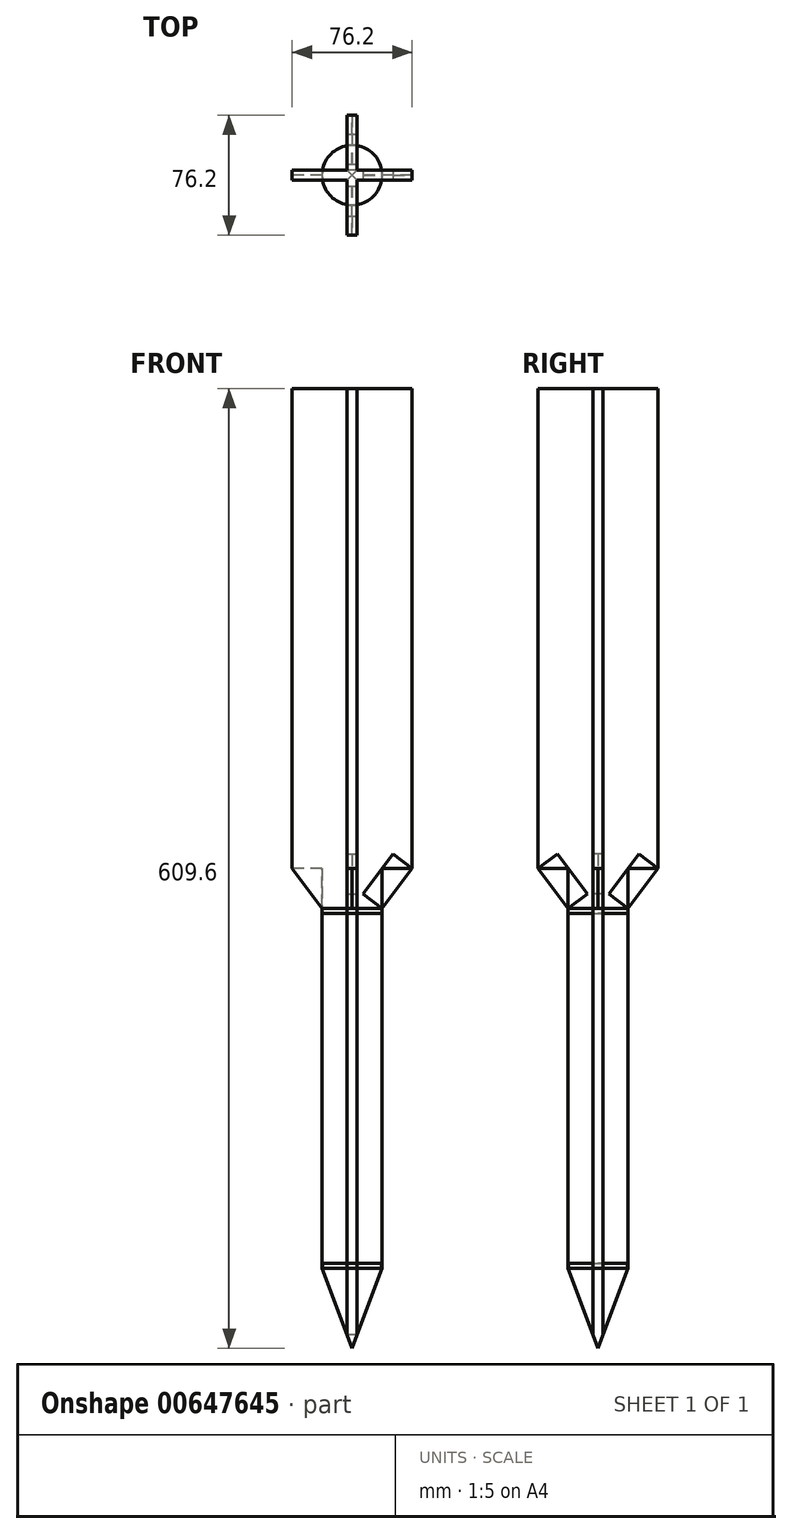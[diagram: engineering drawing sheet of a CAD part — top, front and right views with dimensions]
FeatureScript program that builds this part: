
annotation { "Feature Type Name" : "Feature", "Feature Type Description" : "" }
export const myFeature = defineFeature(function(context is Context, id is Id, definition is map)
    precondition{}
    {
        {
            var Q0;
            Q0=qCreatedBy(makeId("Top.planeOp"),FACE);
            var sketch = newSketch(context, id + "F0", { "sketchPlane" : qUnion([Q0])});
            skLineSegment(sketch, "E0.bottom", {"start": v(3.18, 38.1) * mm, "end": v(-3.17, 38.1) * mm});
            skLineSegment(sketch, "E0.top", {"start": v(3.18, -38.1) * mm, "end": v(-3.18, -38.1) * mm});
            skLineSegment(sketch, "E0.left", {"start": v(3.18, 38.1) * mm, "end": v(3.18, -38.1) * mm});
            skLineSegment(sketch, "E0.right", {"start": v(-3.17, 38.1) * mm, "end": v(-3.18, -38.1) * mm});
            skPoint(sketch, "E0.middle", {"position": v(0, 0) * mm});
            skLineSegment(sketch, "E1.bottom", {"start": v(38.1, -3.17) * mm, "end": v(-38.1, -3.18) * mm});
            skLineSegment(sketch, "E1.top", {"start": v(38.1, 3.18) * mm, "end": v(-38.1, 3.18) * mm});
            skLineSegment(sketch, "E1.left", {"start": v(38.1, -3.17) * mm, "end": v(38.1, 3.18) * mm});
            skLineSegment(sketch, "E1.right", {"start": v(-38.1, -3.18) * mm, "end": v(-38.1, 3.18) * mm});
            skSolve(sketch);
        }
        {
            var Q0;
            {var subQ0=sQuery(id+"F0.wireOp",EDGE,"E0.bottom");Q0=makeQuery(id+"F0.imprint","IMPRINT",FACE,{"disambiguationData":[TD([[makeQuery(id+"F0.imprint","IMPRINT",EDGE,{"derivedFrom":subQ0}),1.0]])]});}
            var Q1;
            {var subQ5=sQuery(id+"F0.wireOp",EDGE,"E1.right");Q1=makeQuery(id+"F0.imprint","IMPRINT",FACE,{"disambiguationData":[TD([[makeQuery(id+"F0.imprint","IMPRINT",EDGE,{"derivedFrom":subQ5}),-1.0]])]});}
            var Q2;
            {var subQ0=sQuery(id+"F0.wireOp",EDGE,"E0.top");Q2=makeQuery(id+"F0.imprint","IMPRINT",FACE,{"disambiguationData":[TD([[makeQuery(id+"F0.imprint","IMPRINT",EDGE,{"derivedFrom":subQ0}),-1.0]])]});}
            var Q3;
            {var subQ0=sQuery(id+"F0.wireOp",EDGE,"E1.top");var subQ1=sQuery(id+"F0.wireOp",EDGE,"E0.left");var subQ2=makeQuery(id+"F0.imprint","INTERSECT",VERTEX,{"derivedFrom":[subQ1,subQ0]});Q3=makeQuery(id+"F0.imprint","IMPRINT",FACE,{"disambiguationData":[TD([[makeQuery(id+"F0.imprint","IMPRINT",EDGE,{"disambiguationData":[TD([[subQ2,-1.0]])],"derivedFrom":subQ1}),-1.0]])]});}
            var Q4;
            {var subQ5=sQuery(id+"F0.wireOp",EDGE,"E1.left");Q4=makeQuery(id+"F0.imprint","IMPRINT",FACE,{"disambiguationData":[TD([[makeQuery(id+"F0.imprint","IMPRINT",EDGE,{"derivedFrom":subQ5}),1.0]])]});}
            extrude(context, id + "F1", {"entities" : qUnion([Q0, Q1, Q2, Q3, Q4]), "depth" : 304.8 * mm, "offsetDistance" : 25.4 * mm});
        }
        {
            var Q0;
            Q0=qCreatedBy(makeId("Top.planeOp"),FACE);
            var sketch = newSketch(context, id + "F2", { "sketchPlane" : qUnion([Q0])});
            skLineSegment(sketch, "E2.bottom", {"start": v(19.05, 3.18) * mm, "end": v(-19.05, 3.17) * mm});
            skLineSegment(sketch, "E2.top", {"start": v(19.05, -3.17) * mm, "end": v(-19.05, -3.18) * mm});
            skLineSegment(sketch, "E2.left", {"start": v(19.05, 3.18) * mm, "end": v(19.05, -3.17) * mm});
            skLineSegment(sketch, "E2.right", {"start": v(-19.05, 3.17) * mm, "end": v(-19.05, -3.18) * mm});
            skPoint(sketch, "E2.middle", {"position": v(0, 0) * mm});
            skLineSegment(sketch, "E3.bottom", {"start": v(3.18, -19.05) * mm, "end": v(-3.18, -19.05) * mm});
            skLineSegment(sketch, "E3.top", {"start": v(3.18, 19.05) * mm, "end": v(-3.17, 19.05) * mm});
            skLineSegment(sketch, "E3.left", {"start": v(3.18, -19.05) * mm, "end": v(3.18, 19.05) * mm});
            skLineSegment(sketch, "E3.right", {"start": v(-3.18, -19.05) * mm, "end": v(-3.17, 19.05) * mm});
            skSolve(sketch);
        }
        {
            var Q0;
            {var subQ0=sQuery(id+"F2.wireOp",EDGE,"E2.left");Q0=makeQuery(id+"F2.imprint","IMPRINT",FACE,{"disambiguationData":[TD([[makeQuery(id+"F2.imprint","IMPRINT",EDGE,{"derivedFrom":subQ0}),-1.0]])]});}
            var Q1;
            {var subQ0=sQuery(id+"F2.wireOp",EDGE,"E2.right");Q1=makeQuery(id+"F2.imprint","IMPRINT",FACE,{"disambiguationData":[TD([[makeQuery(id+"F2.imprint","IMPRINT",EDGE,{"derivedFrom":subQ0}),1.0]])]});}
            var Q2;
            {var subQ5=sQuery(id+"F2.wireOp",EDGE,"E3.top");Q2=makeQuery(id+"F2.imprint","IMPRINT",FACE,{"disambiguationData":[TD([[makeQuery(id+"F2.imprint","IMPRINT",EDGE,{"derivedFrom":subQ5}),1.0]])]});}
            var Q3;
            {var subQ5=sQuery(id+"F2.wireOp",EDGE,"E3.bottom");Q3=makeQuery(id+"F2.imprint","IMPRINT",FACE,{"disambiguationData":[TD([[makeQuery(id+"F2.imprint","IMPRINT",EDGE,{"derivedFrom":subQ5}),-1.0]])]});}
            var Q4;
            {var subQ0=sQuery(id+"F2.wireOp",EDGE,"E3.left");var subQ1=sQuery(id+"F2.wireOp",EDGE,"E2.bottom");var subQ2=makeQuery(id+"F2.imprint","INTERSECT",VERTEX,{"derivedFrom":[subQ1,subQ0]});Q4=makeQuery(id+"F2.imprint","IMPRINT",FACE,{"disambiguationData":[TD([[makeQuery(id+"F2.imprint","IMPRINT",EDGE,{"disambiguationData":[TD([[subQ2,-1.0]])],"derivedFrom":subQ1}),1.0]])]});}
            extrude(context, id + "F3", {"entities" : qUnion([Q0, Q1, Q2, Q3, Q4]), "oppositeDirection" : true, "depth" : 254 * mm, "offsetDistance" : 25.4 * mm});
        }
        {
            var Q0;
            Q0=qCreatedBy(makeId("Front.planeOp"),FACE);
            var sketch = newSketch(context, id + "F4", { "sketchPlane" : qUnion([Q0])});
            skLineSegment(sketch, "E4", {"start": v(38.1, 0) * mm, "end": v(19.07, -25.4) * mm});
            skSolve(sketch);
        }
        {
            var Q0;
            Q0=sQuery(id+"F4.wireOp",EDGE,"E4");
            extrude(context, id + "F5", {"bodyType" : ToolBodyType.SURFACE, "surfaceEntities" : qUnion([Q0]), "depth" : 3.17 * mm, "offsetDistance" : 25.4 * mm});
        }
        {
            var Q0;
            Q0=makeQuery(id+"F5.opExtrude","SWEPT_FACE",FACE,{"disambiguationData":[OSD([sQuery(id+"F4.wireOp",EDGE,"E4")])]});
            extrude(context, id + "F6", {"entities" : qUnion([Q0]), "depth" : 15.24 * mm, "offsetDistance" : 25.4 * mm});
        }
        {
            var Q0;
            {var subQ0=sQuery(id+"F4.wireOp",EDGE,"E4");Q0=makeQuery(id+"F6.opExtrude","SWEPT_FACE",FACE,{"disambiguationData":[OSD([subQ0]),TDD([makeQuery(id+"F5.opExtrude","CAP_EDGE",EDGE,{"disambiguationData":[OSD([subQ0])],"isStart":true})])]});}
            extrude(context, id + "F7", {"entities" : qUnion([Q0]), "depth" : 3.17 * mm, "offsetDistance" : 25.4 * mm});
        }
        {
            var Q0;
            Q0=qCreatedBy(makeId("Front.planeOp"),FACE);
            var sketch = newSketch(context, id + "F8", { "sketchPlane" : qUnion([Q0])});
            skLineSegment(sketch, "E5", {"start": v(-38.1, 0) * mm, "end": v(-18.93, -25.4) * mm});
            skSolve(sketch);
        }
        {
            var Q0;
            Q0 = qSketchRegion(id + "F8", true);
            var Q1;
            Q1=sQuery(id+"F8.wireOp",EDGE,"E5");
            extrude(context, id + "F9", {"entities" : qUnion([Q0]), "bodyType" : ToolBodyType.SURFACE, "surfaceEntities" : qUnion([Q1]), "depth" : 3.17 * mm, "offsetDistance" : 25.4 * mm});
        }
        {
            var Q0;
            Q0=makeQuery(id+"F9.opExtrude","SWEPT_FACE",FACE,{"disambiguationData":[OSD([sQuery(id+"F8.wireOp",EDGE,"E5")])]});
            extrude(context, id + "F10", {"entities" : qUnion([Q0]), "operationType" : NewBodyOperationType.ADD, "oppositeDirection" : true, "depth" : 15.24 * mm, "offsetDistance" : 25.4 * mm});
        }
        {
            var Q0;
            {var subQ0=sQuery(id+"F8.wireOp",EDGE,"E5");Q0=makeQuery(id+"F10.opExtrude","SWEPT_FACE",FACE,{"disambiguationData":[OSD([subQ0]),TDD([makeQuery(id+"F9.opExtrude","CAP_EDGE",EDGE,{"disambiguationData":[OSD([subQ0])],"isStart":true})])]});}
            extrude(context, id + "F11", {"entities" : qUnion([Q0]), "depth" : 3.17 * mm, "offsetDistance" : 25.4 * mm});
        }
        {
            var Q0;
            Q0=qCreatedBy(makeId("Right.planeOp"),FACE);
            var sketch = newSketch(context, id + "F12", { "sketchPlane" : qUnion([Q0])});
            skLineSegment(sketch, "E6", {"start": v(38.1, 0) * mm, "end": v(19.05, -25.4) * mm});
            skLineSegment(sketch, "E7", {"start": v(-38.1, 0) * mm, "end": v(-19.05, -25.4) * mm});
            skSolve(sketch);
        }
        {
            var Q0;
            Q0 = qSketchRegion(id + "F12", true);
            var Q1;
            Q1=sQuery(id+"F12.wireOp",EDGE,"E6");
            extrude(context, id + "F13", {"entities" : qUnion([Q0]), "bodyType" : ToolBodyType.SURFACE, "surfaceEntities" : qUnion([Q1]), "depth" : 3.17 * mm, "offsetDistance" : 25.4 * mm});
        }
        {
            var Q0;
            Q0=makeQuery(id+"F13.opExtrude","SWEPT_FACE",FACE,{"disambiguationData":[OSD([sQuery(id+"F12.wireOp",EDGE,"E6")])]});
            extrude(context, id + "F14", {"entities" : qUnion([Q0]), "depth" : 15.24 * mm, "offsetDistance" : 25.4 * mm});
        }
        {
            var Q0;
            {var subQ0=sQuery(id+"F12.wireOp",EDGE,"E6");Q0=makeQuery(id+"F14.opExtrude","SWEPT_FACE",FACE,{"disambiguationData":[OSD([subQ0]),TDD([makeQuery(id+"F13.opExtrude","CAP_EDGE",EDGE,{"disambiguationData":[OSD([subQ0])],"isStart":true})])]});}
            extrude(context, id + "F15", {"entities" : qUnion([Q0]), "depth" : 3.17 * mm, "offsetDistance" : 25.4 * mm});
        }
        {
            var Q0;
            Q0=sQuery(id+"F12.wireOp",EDGE,"E7");
            extrude(context, id + "F16", {"bodyType" : ToolBodyType.SURFACE, "surfaceEntities" : qUnion([Q0]), "depth" : 3.17 * mm, "offsetDistance" : 25.4 * mm});
        }
        {
            var Q0;
            Q0=makeQuery(id+"F16.opExtrude","SWEPT_FACE",FACE,{"disambiguationData":[OSD([sQuery(id+"F12.wireOp",EDGE,"E7")])]});
            extrude(context, id + "F17", {"entities" : qUnion([Q0]), "oppositeDirection" : true, "depth" : 15.24 * mm, "offsetDistance" : 25.4 * mm});
        }
        {
            var Q0;
            {var subQ0=sQuery(id+"F12.wireOp",EDGE,"E7");Q0=makeQuery(id+"F17.opExtrude","SWEPT_FACE",FACE,{"disambiguationData":[OSD([subQ0]),TDD([makeQuery(id+"F16.opExtrude","CAP_EDGE",EDGE,{"disambiguationData":[OSD([subQ0])],"isStart":true})])]});}
            extrude(context, id + "F18", {"entities" : qUnion([Q0]), "depth" : 3.17 * mm, "offsetDistance" : 25.4 * mm});
        }
        {
            var Q0;
            Q0=qCreatedBy(makeId("Top.planeOp"),FACE);
            var sketch = newSketch(context, id + "F19", { "sketchPlane" : qUnion([Q0])});
            skCircle(sketch, "E8", {"center": v(0, 0) * mm, "radius": 19.05 * mm});
            skSolve(sketch);
        }
        {
            var Q0;
            Q0=makeQuery(id+"F19.imprint","IMPRINT",FACE,{"disambiguationData":[TD([[makeQuery(id+"F19.imprint","IMPRINT",EDGE,{"derivedFrom":sQuery(id+"F19.wireOp",EDGE,"E8")}),1.0]])]});
            extrude(context, id + "F20", {"entities" : qUnion([Q0]), "oppositeDirection" : true, "depth" : 250.82 * mm, "offsetDistance" : 25.4 * mm, "hasSecondDirection" : true, "secondDirectionOppositeDirection" : true, "secondDirectionDepth" : 28.57 * mm});
        }
        {
            var Q0;
            Q0=qCreatedBy(makeId("Top.planeOp"),FACE);
            var sketch = newSketch(context, id + "F21", { "sketchPlane" : qUnion([Q0])});
            skCircle(sketch, "E9", {"center": v(0, 0) * mm, "radius": 19.05 * mm});
            skSolve(sketch);
        }
        {
            var Q0;
            Q0=makeQuery(id+"F21.imprint","IMPRINT",FACE,{"disambiguationData":[TD([[makeQuery(id+"F21.imprint","IMPRINT",EDGE,{"derivedFrom":sQuery(id+"F21.wireOp",EDGE,"E9")}),1.0]])]});
            extrude(context, id + "F22", {"entities" : qUnion([Q0]), "oppositeDirection" : true, "depth" : 28.57 * mm, "offsetDistance" : 25.4 * mm, "hasSecondDirection" : true, "secondDirectionOppositeDirection" : true, "secondDirectionDepth" : 25.4 * mm});
        }
        {
            var Q0;
            Q0=qCreatedBy(makeId("Top.planeOp"),FACE);
            var sketch = newSketch(context, id + "F23", { "sketchPlane" : qUnion([Q0])});
            skCircle(sketch, "E10", {"center": v(0, 0) * mm, "radius": 19.05 * mm});
            skSolve(sketch);
        }
        {
            var Q0;
            Q0=makeQuery(id+"F23.imprint","IMPRINT",FACE,{"disambiguationData":[TD([[makeQuery(id+"F23.imprint","IMPRINT",EDGE,{"derivedFrom":sQuery(id+"F23.wireOp",EDGE,"E10")}),1.0]])]});
            extrude(context, id + "F24", {"entities" : qUnion([Q0]), "oppositeDirection" : true, "depth" : 254 * mm, "offsetDistance" : 25.4 * mm, "hasSecondDirection" : true, "secondDirectionOppositeDirection" : true, "secondDirectionDepth" : 250.82 * mm});
        }
        {
            var Q0;
            Q0=qCreatedBy(makeId("Front.planeOp"),FACE);
            var sketch = newSketch(context, id + "F25", { "sketchPlane" : qUnion([Q0])});
            skLineSegment(sketch, "E11", {"start": v(19.05, -254) * mm, "end": v(0, -304.8) * mm});
            skLineSegment(sketch, "E12", {"start": v(0, -304.8) * mm, "end": v(-19.05, -254) * mm});
            skLineSegment(sketch, "E13", {"start": v(19.05, -254) * mm, "end": v(-19.05, -254) * mm});
            skSolve(sketch);
        }
        {
            var Q0;
            Q0 = qSketchRegion(id + "F25", true);
            extrude(context, id + "F26", {"entities" : qUnion([Q0]), "operationType" : NewBodyOperationType.ADD, "depth" : 3.17 * mm, "offsetDistance" : 25.4 * mm, "hasSecondDirection" : true, "secondDirectionOppositeDirection" : true, "secondDirectionDepth" : 3.17 * mm});
        }
        {
            var Q0;
            Q0=qCreatedBy(makeId("Right.planeOp"),FACE);
            var sketch = newSketch(context, id + "F27", { "sketchPlane" : qUnion([Q0])});
            skLineSegment(sketch, "E14", {"start": v(-19.05, -254) * mm, "end": v(0, -304.8) * mm});
            skLineSegment(sketch, "E15", {"start": v(0, -304.8) * mm, "end": v(19.05, -253.96) * mm});
            skLineSegment(sketch, "E16", {"start": v(19.05, -253.96) * mm, "end": v(-19.05, -254) * mm});
            skSolve(sketch);
        }
        {
            var Q0;
            Q0 = qSketchRegion(id + "F27", true);
            extrude(context, id + "F28", {"entities" : qUnion([Q0]), "operationType" : NewBodyOperationType.ADD, "depth" : 3.17 * mm, "offsetDistance" : 25.4 * mm, "hasSecondDirection" : true, "secondDirectionOppositeDirection" : true, "secondDirectionDepth" : 3.17 * mm});
        }
        {
            var Q0;
            Q0=qCreatedBy(makeId("Front.planeOp"),FACE);
            var sketch = newSketch(context, id + "F29", { "sketchPlane" : qUnion([Q0])});
            skLineSegment(sketch, "E17", {"start": v(19.05, -254) * mm, "end": v(0, -304.8) * mm});
            skLineSegment(sketch, "E18", {"start": v(0, -304.8) * mm, "end": v(14.5, -306.95) * mm});
            skLineSegment(sketch, "E19", {"start": v(14.5, -306.95) * mm, "end": v(19.05, -254) * mm});
            skSolve(sketch);
        }
        {
            var Q0;
            Q0 = qSketchRegion(id + "F29", true);
            extrude(context, id + "F30", {"entities" : qUnion([Q0]), "operationType" : NewBodyOperationType.REMOVE, "oppositeDirection" : true, "depth" : 25.4 * mm, "offsetDistance" : 25.4 * mm, "hasSecondDirection" : true, "secondDirectionOppositeDirection" : false, "secondDirectionDepth" : 25.4 * mm});
        }
        {
            var Q0;
            Q0=qCreatedBy(makeId("Front.planeOp"),FACE);
            var sketch = newSketch(context, id + "F31", { "sketchPlane" : qUnion([Q0])});
            skLineSegment(sketch, "E20", {"start": v(-19.05, -254) * mm, "end": v(0, -304.8) * mm});
            skLineSegment(sketch, "E21", {"start": v(0, -304.8) * mm, "end": v(-18, -308.15) * mm});
            skLineSegment(sketch, "E22", {"start": v(-18, -308.15) * mm, "end": v(-19.05, -254) * mm});
            skSolve(sketch);
        }
        {
            var Q0;
            Q0 = qSketchRegion(id + "F31", true);
            extrude(context, id + "F32", {"entities" : qUnion([Q0]), "operationType" : NewBodyOperationType.REMOVE, "oppositeDirection" : true, "depth" : 25.4 * mm, "offsetDistance" : 25.4 * mm, "hasSecondDirection" : true, "secondDirectionOppositeDirection" : false, "secondDirectionDepth" : 25.4 * mm});
        }
        {
            var Q0;
            Q0=qCreatedBy(makeId("Right.planeOp"),FACE);
            var sketch = newSketch(context, id + "F33", { "sketchPlane" : qUnion([Q0])});
            skLineSegment(sketch, "E23", {"start": v(-19.05, -254) * mm, "end": v(0, -304.8) * mm});
            skLineSegment(sketch, "E24", {"start": v(0, -304.8) * mm, "end": v(-21.65, -304.8) * mm});
            skLineSegment(sketch, "E25", {"start": v(-21.65, -304.8) * mm, "end": v(-19.43, -254.48) * mm});
            skLineSegment(sketch, "E26", {"start": v(-19.43, -254.48) * mm, "end": v(-18.88, -253.97) * mm});
            skSolve(sketch);
        }
        {
            var Q0;
            Q0 = qSketchRegion(id + "F33", true);
            extrude(context, id + "F34", {"entities" : qUnion([Q0]), "operationType" : NewBodyOperationType.REMOVE, "oppositeDirection" : true, "depth" : 25.4 * mm, "offsetDistance" : 25.4 * mm, "hasSecondDirection" : true, "secondDirectionOppositeDirection" : false, "secondDirectionDepth" : 25.4 * mm});
        }
        {
            var Q0;
            Q0=qCreatedBy(makeId("Right.planeOp"),FACE);
            var sketch = newSketch(context, id + "F35", { "sketchPlane" : qUnion([Q0])});
            skLineSegment(sketch, "E27", {"start": v(19.05, -254) * mm, "end": v(0, -304.8) * mm});
            skLineSegment(sketch, "E28", {"start": v(0, -304.8) * mm, "end": v(28.51, -304.8) * mm});
            skLineSegment(sketch, "E29", {"start": v(19.05, -254) * mm, "end": v(28.51, -304.8) * mm});
            skSolve(sketch);
        }
        {
            var Q0;
            Q0 = qSketchRegion(id + "F35", true);
            extrude(context, id + "F36", {"entities" : qUnion([Q0]), "operationType" : NewBodyOperationType.REMOVE, "oppositeDirection" : true, "depth" : 25.4 * mm, "offsetDistance" : 25.4 * mm, "hasSecondDirection" : true, "secondDirectionOppositeDirection" : false, "secondDirectionDepth" : 25.4 * mm});
        }
    });
